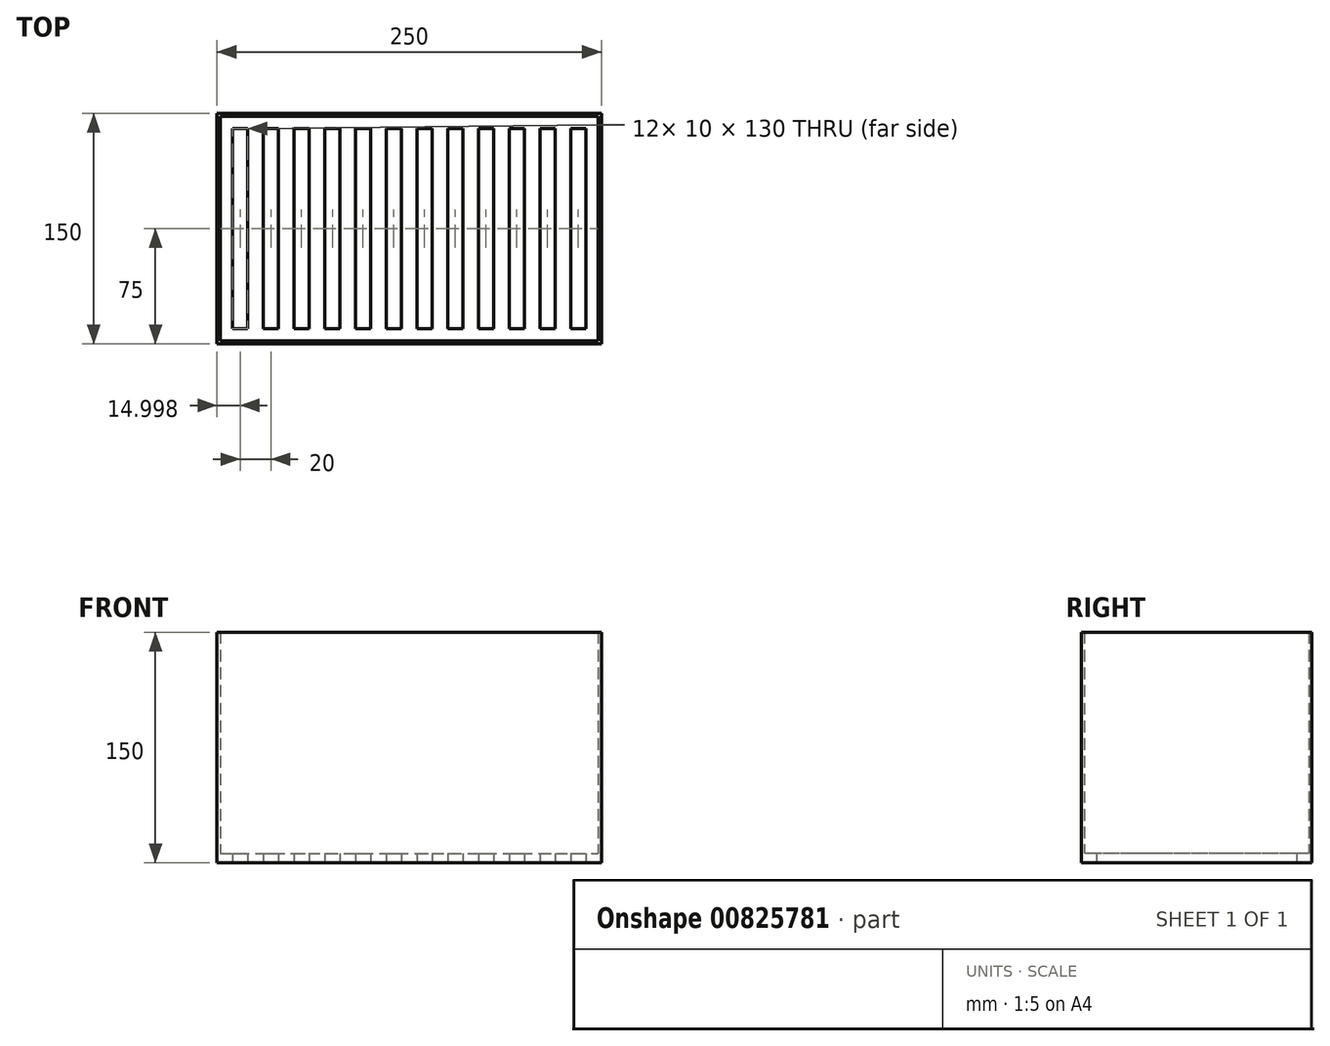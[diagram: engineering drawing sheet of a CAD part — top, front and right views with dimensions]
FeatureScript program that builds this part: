
annotation { "Feature Type Name" : "Feature", "Feature Type Description" : "" }
export const myFeature = defineFeature(function(context is Context, id is Id, definition is map)
    precondition{}
    {
        {
            var Q0;
            Q0=qCreatedBy(makeId("Top.planeOp"),FACE);
            var sketch = newSketch(context, id + "F0", { "sketchPlane" : qUnion([Q0])});
            skLineSegment(sketch, "E0.bottom", {"start": v(-143.32, 73.34) * mm, "end": v(106.68, 73.34) * mm});
            skLineSegment(sketch, "E0.top", {"start": v(-143.32, -76.66) * mm, "end": v(106.68, -76.66) * mm});
            skLineSegment(sketch, "E0.left", {"start": v(-143.32, 73.34) * mm, "end": v(-143.32, -76.66) * mm});
            skLineSegment(sketch, "E0.right", {"start": v(106.68, 73.34) * mm, "end": v(106.68, -76.66) * mm});
            skLineSegment(sketch, "E1.bottom", {"start": v(-133.32, 63.34) * mm, "end": v(-123.32, 63.34) * mm});
            skLineSegment(sketch, "E1.top", {"start": v(-133.32, -66.66) * mm, "end": v(-123.32, -66.66) * mm});
            skLineSegment(sketch, "E1.left", {"start": v(-133.32, 63.34) * mm, "end": v(-133.32, -66.66) * mm});
            skLineSegment(sketch, "E1.right", {"start": v(-123.32, 63.34) * mm, "end": v(-123.32, -66.66) * mm});
            skLineSegment(sketch, "E2.1.0.0", {"start": v(-103.32, 63.34) * mm, "end": v(-103.32, -66.66) * mm});
            skLineSegment(sketch, "E2.1.0.1", {"start": v(-113.32, 63.34) * mm, "end": v(-103.32, 63.34) * mm});
            skLineSegment(sketch, "E2.1.0.2", {"start": v(-113.32, 63.34) * mm, "end": v(-113.32, -66.66) * mm});
            skLineSegment(sketch, "E2.1.0.3", {"start": v(-113.32, -66.66) * mm, "end": v(-103.32, -66.66) * mm});
            skLineSegment(sketch, "E2.2.0.0", {"start": v(-83.32, 63.34) * mm, "end": v(-83.32, -66.66) * mm});
            skLineSegment(sketch, "E2.2.0.1", {"start": v(-93.32, 63.34) * mm, "end": v(-83.32, 63.34) * mm});
            skLineSegment(sketch, "E2.2.0.2", {"start": v(-93.32, 63.34) * mm, "end": v(-93.32, -66.66) * mm});
            skLineSegment(sketch, "E2.2.0.3", {"start": v(-93.32, -66.66) * mm, "end": v(-83.32, -66.66) * mm});
            skLineSegment(sketch, "E2.3.0.0", {"start": v(-63.32, 63.34) * mm, "end": v(-63.32, -66.66) * mm});
            skLineSegment(sketch, "E2.3.0.1", {"start": v(-73.32, 63.34) * mm, "end": v(-63.32, 63.34) * mm});
            skLineSegment(sketch, "E2.3.0.2", {"start": v(-73.32, 63.34) * mm, "end": v(-73.32, -66.66) * mm});
            skLineSegment(sketch, "E2.3.0.3", {"start": v(-73.32, -66.66) * mm, "end": v(-63.32, -66.66) * mm});
            skLineSegment(sketch, "E2.4.0.0", {"start": v(-43.32, 63.34) * mm, "end": v(-43.32, -66.66) * mm});
            skLineSegment(sketch, "E2.4.0.1", {"start": v(-53.32, 63.34) * mm, "end": v(-43.32, 63.34) * mm});
            skLineSegment(sketch, "E2.4.0.2", {"start": v(-53.32, 63.34) * mm, "end": v(-53.32, -66.66) * mm});
            skLineSegment(sketch, "E2.4.0.3", {"start": v(-53.32, -66.66) * mm, "end": v(-43.32, -66.66) * mm});
            skLineSegment(sketch, "E2.5.0.0", {"start": v(-23.32, 63.34) * mm, "end": v(-23.32, -66.66) * mm});
            skLineSegment(sketch, "E2.5.0.1", {"start": v(-33.32, 63.34) * mm, "end": v(-23.32, 63.34) * mm});
            skLineSegment(sketch, "E2.5.0.2", {"start": v(-33.32, 63.34) * mm, "end": v(-33.32, -66.66) * mm});
            skLineSegment(sketch, "E2.5.0.3", {"start": v(-33.32, -66.66) * mm, "end": v(-23.32, -66.66) * mm});
            skLineSegment(sketch, "E2.6.0.0", {"start": v(-3.32, 63.34) * mm, "end": v(-3.32, -66.66) * mm});
            skLineSegment(sketch, "E2.6.0.1", {"start": v(-13.32, 63.34) * mm, "end": v(-3.32, 63.34) * mm});
            skLineSegment(sketch, "E2.6.0.2", {"start": v(-13.32, 63.34) * mm, "end": v(-13.32, -66.66) * mm});
            skLineSegment(sketch, "E2.6.0.3", {"start": v(-13.32, -66.66) * mm, "end": v(-3.32, -66.66) * mm});
            skLineSegment(sketch, "E2.7.0.0", {"start": v(16.68, 63.34) * mm, "end": v(16.68, -66.66) * mm});
            skLineSegment(sketch, "E2.7.0.1", {"start": v(6.68, 63.34) * mm, "end": v(16.68, 63.34) * mm});
            skLineSegment(sketch, "E2.7.0.2", {"start": v(6.68, 63.34) * mm, "end": v(6.68, -66.66) * mm});
            skLineSegment(sketch, "E2.7.0.3", {"start": v(6.68, -66.66) * mm, "end": v(16.68, -66.66) * mm});
            skLineSegment(sketch, "E2.8.0.0", {"start": v(36.68, 63.34) * mm, "end": v(36.68, -66.66) * mm});
            skLineSegment(sketch, "E2.8.0.1", {"start": v(26.68, 63.34) * mm, "end": v(36.68, 63.34) * mm});
            skLineSegment(sketch, "E2.8.0.2", {"start": v(26.68, 63.34) * mm, "end": v(26.68, -66.66) * mm});
            skLineSegment(sketch, "E2.8.0.3", {"start": v(26.68, -66.66) * mm, "end": v(36.68, -66.66) * mm});
            skLineSegment(sketch, "E2.9.0.0", {"start": v(56.68, 63.34) * mm, "end": v(56.68, -66.66) * mm});
            skLineSegment(sketch, "E2.9.0.1", {"start": v(46.68, 63.34) * mm, "end": v(56.68, 63.34) * mm});
            skLineSegment(sketch, "E2.9.0.2", {"start": v(46.68, 63.34) * mm, "end": v(46.68, -66.66) * mm});
            skLineSegment(sketch, "E2.9.0.3", {"start": v(46.68, -66.66) * mm, "end": v(56.68, -66.66) * mm});
            skLineSegment(sketch, "E2.10.0.0", {"start": v(76.68, 63.34) * mm, "end": v(76.68, -66.66) * mm});
            skLineSegment(sketch, "E2.10.0.1", {"start": v(66.68, 63.34) * mm, "end": v(76.68, 63.34) * mm});
            skLineSegment(sketch, "E2.10.0.2", {"start": v(66.68, 63.34) * mm, "end": v(66.68, -66.66) * mm});
            skLineSegment(sketch, "E2.10.0.3", {"start": v(66.68, -66.66) * mm, "end": v(76.68, -66.66) * mm});
            skLineSegment(sketch, "E2.11.0.0", {"start": v(96.68, 63.34) * mm, "end": v(96.68, -66.66) * mm});
            skLineSegment(sketch, "E2.11.0.1", {"start": v(86.68, 63.34) * mm, "end": v(96.68, 63.34) * mm});
            skLineSegment(sketch, "E2.11.0.2", {"start": v(86.68, 63.34) * mm, "end": v(86.68, -66.66) * mm});
            skLineSegment(sketch, "E2.11.0.3", {"start": v(86.68, -66.66) * mm, "end": v(96.68, -66.66) * mm});
            skLineSegment(sketch, "E2.direction1", {"start": v(-123.32, -66.66) * mm, "end": v(-103.32, -66.66) * mm, "construction": true});
            skSolve(sketch);
        }
        {
            var Q0;
            Q0=makeQuery(id+"F0.imprint","IMPRINT",FACE,{"disambiguationData":[TD([[makeQuery(id+"F0.imprint","IMPRINT",EDGE,{"derivedFrom":sQuery(id+"F0.wireOp",EDGE,"E0.bottom")}),-1.0]])]});
            var sketch = newSketch(context, id + "F1", { "sketchPlane" : qUnion([Q0])});
            skLineSegment(sketch, "E3.bottom", {"start": v(-141.32, 71.34) * mm, "end": v(104.68, 71.34) * mm});
            skLineSegment(sketch, "E3.top", {"start": v(-141.32, -74.66) * mm, "end": v(104.68, -74.66) * mm});
            skLineSegment(sketch, "E3.left", {"start": v(-141.32, 71.34) * mm, "end": v(-141.32, -74.66) * mm});
            skLineSegment(sketch, "E3.right", {"start": v(104.68, 71.34) * mm, "end": v(104.68, -74.66) * mm});
            skLineSegment(sketch, "E4.bottom", {"start": v(-143.33, 73.34) * mm, "end": v(106.68, 73.34) * mm});
            skLineSegment(sketch, "E4.top", {"start": v(-143.33, -76.66) * mm, "end": v(106.68, -76.66) * mm});
            skLineSegment(sketch, "E4.left", {"start": v(-143.33, 73.34) * mm, "end": v(-143.33, -76.66) * mm});
            skLineSegment(sketch, "E4.right", {"start": v(106.68, 73.34) * mm, "end": v(106.68, -76.66) * mm});
            skSolve(sketch);
        }
        {
            var Q0;
            Q0=makeQuery(id+"F1.imprint","IMPRINT",FACE,{"disambiguationData":[TD([[makeQuery(id+"F1.imprint","IMPRINT",EDGE,{"derivedFrom":sQuery(id+"F1.wireOp",EDGE,"E3.bottom")}),-1.0]])]});
            extrude(context, id + "F2", {"entities" : qUnion([Q0]), "depth" : 6 * mm, "offsetDistance" : 25 * mm});
        }
        {
            var Q0;
            Q0=makeQuery(id+"F1.imprint","IMPRINT",FACE,{"disambiguationData":[TD([[makeQuery(id+"F1.imprint","IMPRINT",EDGE,{"derivedFrom":sQuery(id+"F1.wireOp",EDGE,"E3.bottom")}),1.0]])]});
            extrude(context, id + "F3", {"entities" : qUnion([Q0]), "operationType" : NewBodyOperationType.ADD, "depth" : 150 * mm, "offsetDistance" : 25 * mm});
        }
    });
